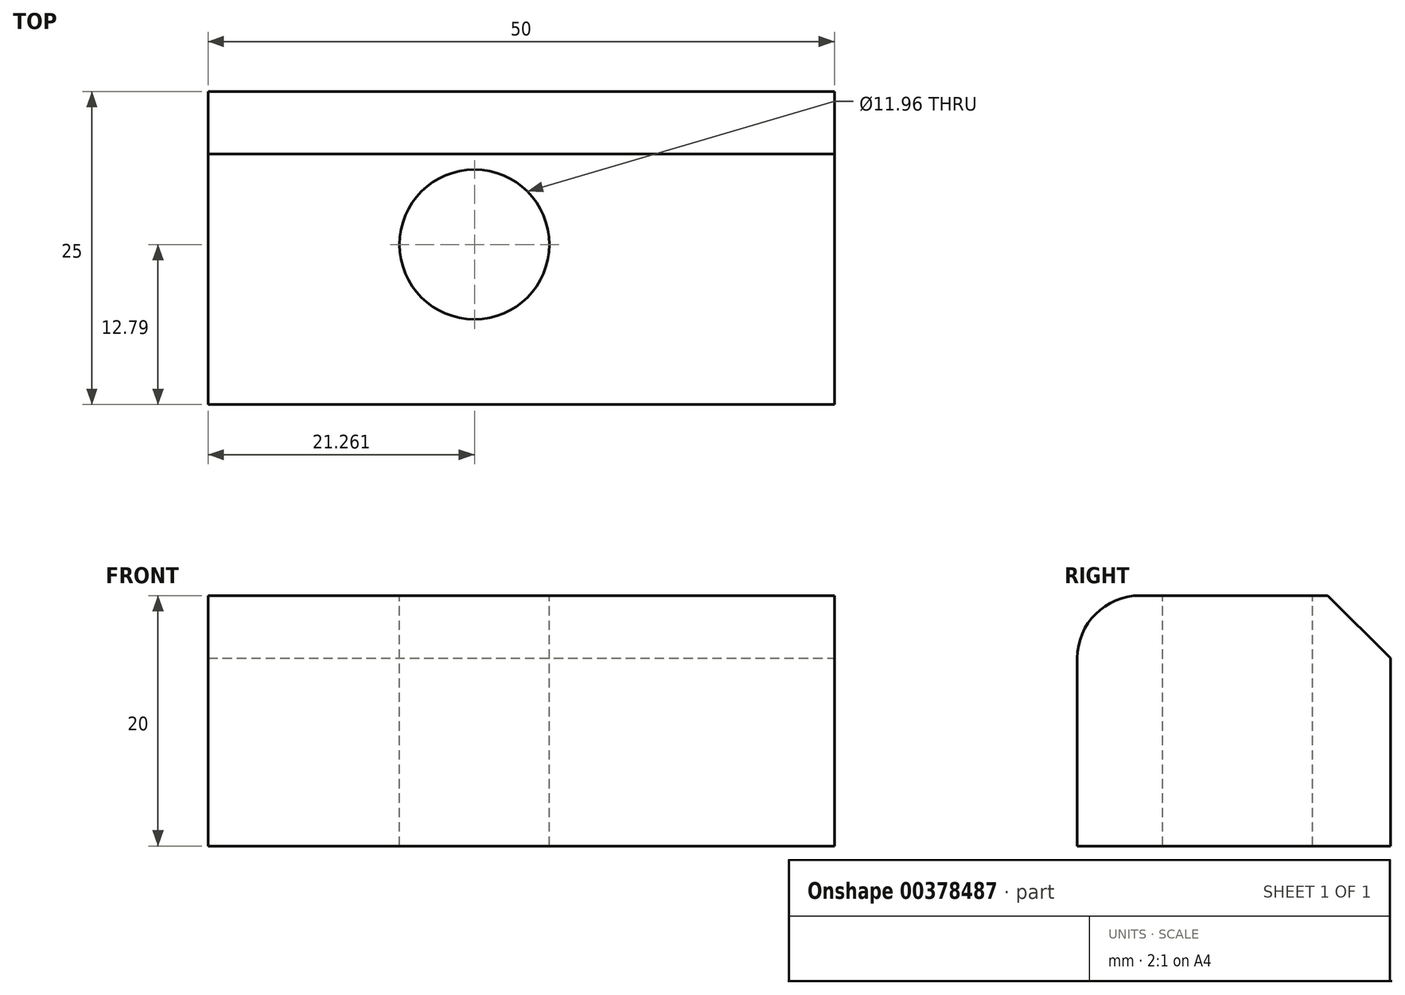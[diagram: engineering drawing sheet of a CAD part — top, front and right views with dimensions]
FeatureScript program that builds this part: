
annotation { "Feature Type Name" : "Feature", "Feature Type Description" : "" }
export const myFeature = defineFeature(function(context is Context, id is Id, definition is map)
    precondition{}
    {
        {
            var Q0;
            Q0=qCreatedBy(makeId("Front.planeOp"),FACE);
            var sketch = newSketch(context, id + "F0", { "sketchPlane" : qUnion([Q0])});
            skLineSegment(sketch, "E0.bottom", {"start": v(-14.54, 18.98) * mm, "end": v(35.46, 18.98) * mm});
            skLineSegment(sketch, "E0.top", {"start": v(-14.54, -1.02) * mm, "end": v(35.46, -1.02) * mm});
            skLineSegment(sketch, "E0.left", {"start": v(-14.54, 18.98) * mm, "end": v(-14.54, -1.02) * mm});
            skLineSegment(sketch, "E0.right", {"start": v(35.46, 18.98) * mm, "end": v(35.46, -1.02) * mm});
            skSolve(sketch);
        }
        {
            var Q0;
            Q0=makeQuery(id+"F0.imprint","IMPRINT",FACE,{"disambiguationData":[TD([[makeQuery(id+"F0.imprint","IMPRINT",EDGE,{"derivedFrom":sQuery(id+"F0.wireOp",EDGE,"E0.bottom")}),-1.0]])]});
            extrude(context, id + "F1", {"entities" : qUnion([Q0]), "depth" : 25 * mm});
        }
        {
            var Q0;
            Q0=makeQuery(id+"F1.opExtrude","CAP_EDGE",EDGE,{"disambiguationData":[OSD([sQuery(id+"F0.wireOp",EDGE,"E0.bottom")])],"isStart":false});
            fillet(context, id + "F2", {"entities" : qUnion([Q0]), "radius" : 5 * mm, "tangentPropagation" : true, "allowEdgeOverflow" : false});
        }
        {
            var Q0;
            Q0=makeQuery(id+"F1.opExtrude","CAP_EDGE",EDGE,{"disambiguationData":[OSD([sQuery(id+"F0.wireOp",EDGE,"E0.bottom")])],"isStart":true});
            chamfer(context, id + "F3", {"entities" : qUnion([Q0]), "width" : 5 * mm, "tangentPropagation" : true});
        }
        {
            var Q0;
            Q0=makeQuery(id+"F1.opExtrude","SWEPT_FACE",FACE,{"disambiguationData":[OSD([sQuery(id+"F0.wireOp",EDGE,"E0.bottom")])]});
            var sketch = newSketch(context, id + "F4", { "sketchPlane" : qUnion([Q0])});
            skCircle(sketch, "E1", {"center": v(6.72, -12.21) * mm, "radius": 5.98 * mm});
            skSolve(sketch);
        }
        {
            var Q0;
            Q0 = qSketchRegion(id + "F4", true);
            extrude(context, id + "F5", {"entities" : qUnion([Q0]), "operationType" : NewBodyOperationType.REMOVE, "oppositeDirection" : true, "depth" : 25 * mm});
        }
    });
